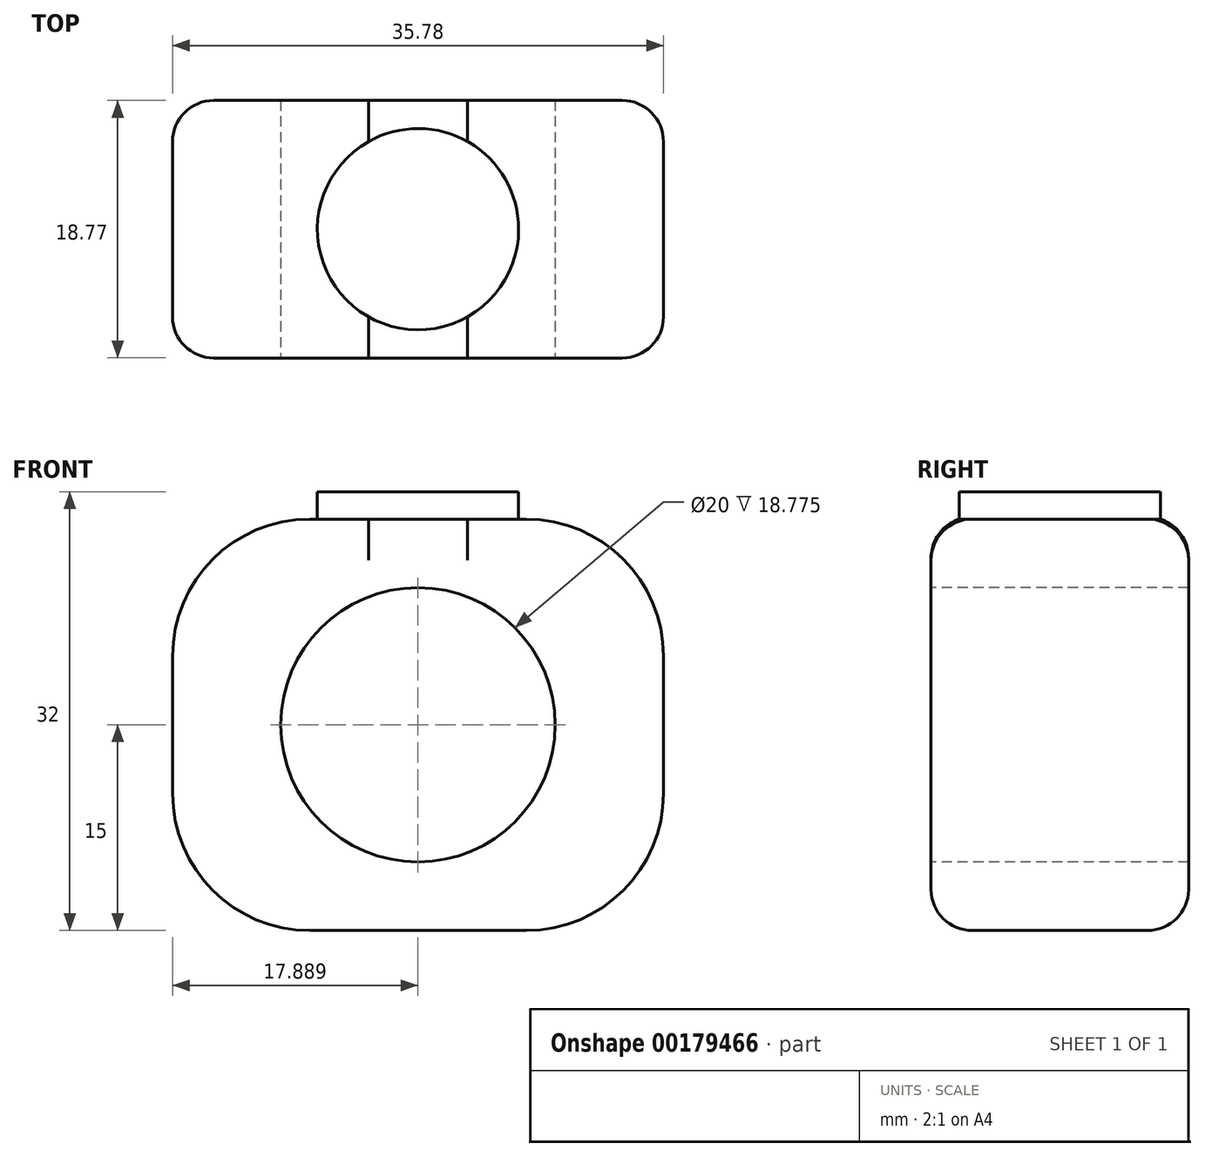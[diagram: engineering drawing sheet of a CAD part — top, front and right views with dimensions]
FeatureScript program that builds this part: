
annotation { "Feature Type Name" : "Feature", "Feature Type Description" : "" }
export const myFeature = defineFeature(function(context is Context, id is Id, definition is map)
    precondition{}
    {
        {
            var Q0;
            Q0=qCreatedBy(makeId("Top.planeOp"),FACE);
            var sketch = newSketch(context, id + "F0", { "sketchPlane" : qUnion([Q0])});
            skLineSegment(sketch, "E0.bottom", {"start": v(-30.93, 23.95) * mm, "end": v(4.85, 23.95) * mm});
            skLineSegment(sketch, "E0.top", {"start": v(-30.93, 5.18) * mm, "end": v(4.85, 5.18) * mm});
            skLineSegment(sketch, "E0.left", {"start": v(-30.93, 23.95) * mm, "end": v(-30.93, 5.18) * mm});
            skLineSegment(sketch, "E0.right", {"start": v(4.85, 23.95) * mm, "end": v(4.85, 5.18) * mm});
            skSolve(sketch);
        }
        {
            var Q0;
            Q0=makeQuery(id+"F0.imprint","IMPRINT",FACE,{"disambiguationData":[TD([[makeQuery(id+"F0.imprint","IMPRINT",EDGE,{"derivedFrom":sQuery(id+"F0.wireOp",EDGE,"E0.bottom")}),-1.0]])]});
            extrude(context, id + "F1", {"entities" : qUnion([Q0]), "depth" : 30 * mm});
        }
        {
            var Q0;
            Q0=makeQuery(id+"F1.opExtrude","SWEPT_FACE",FACE,{"disambiguationData":[OSD([sQuery(id+"F0.wireOp",EDGE,"E0.top")])]});
            var sketch = newSketch(context, id + "F2", { "sketchPlane" : qUnion([Q0])});
            skCircle(sketch, "E1", {"center": v(-13.04, 15) * mm, "radius": 10 * mm});
            skLineSegment(sketch, "E2", {"start": v(-30.93, 15) * mm, "end": v(4.85, 15) * mm});
            skLineSegment(sketch, "E3", {"start": v(-13.04, 15) * mm, "end": v(-13.04, -0.72) * mm});
            skSolve(sketch);
        }
        {
            var Q0;
            Q0=makeQuery(id+"F2.imprint","IMPRINT",FACE,{"disambiguationData":[TD([[makeQuery(id+"F2.imprint","IMPRINT",EDGE,{"derivedFrom":sQuery(id+"F2.wireOp",EDGE,"E1")}),1.0]])]});
            extrude(context, id + "F3", {"entities" : qUnion([Q0]), "operationType" : NewBodyOperationType.REMOVE, "oppositeDirection" : true, "depth" : 25 * mm});
        }
        {
            var Q0;
            Q0=makeQuery(id+"F1.opExtrude","CAP_FACE",FACE,{"disambiguationData":[OSD([sQuery(id+"F0.wireOp",EDGE,"E0.bottom"),sQuery(id+"F0.wireOp",EDGE,"E0.top"),sQuery(id+"F0.wireOp",EDGE,"E0.left"),sQuery(id+"F0.wireOp",EDGE,"E0.right")])],"isStart":false});
            var sketch = newSketch(context, id + "F4", { "sketchPlane" : qUnion([Q0])});
            skLineSegment(sketch, "E4", {"start": v(-30.93, 14.56) * mm, "end": v(4.85, 14.56) * mm});
            skCircle(sketch, "E5", {"center": v(-13.04, 14.56) * mm, "radius": 7.34 * mm});
            skSolve(sketch);
        }
        {
            var Q0;
            {var subQ0=sQuery(id+"F4.wireOp",EDGE,"E5");var subQ1=sQuery(id+"F4.wireOp",EDGE,"E4");var subQ2=makeQuery(id+"F4.imprint","INTERSECT",VERTEX,{"disambiguationData":[OD(0.0)],"derivedFrom":[subQ1,subQ0]});Q0=makeQuery(id+"F4.imprint","IMPRINT",FACE,{"disambiguationData":[TD([[makeQuery(id+"F4.imprint","IMPRINT",EDGE,{"disambiguationData":[TD([[subQ2,-1.0]])],"derivedFrom":subQ1}),1.0]])]});}
            var Q1;
            {var subQ0=sQuery(id+"F4.wireOp",EDGE,"E5");var subQ1=sQuery(id+"F4.wireOp",EDGE,"E4");var subQ2=makeQuery(id+"F4.imprint","INTERSECT",VERTEX,{"disambiguationData":[OD(0.0)],"derivedFrom":[subQ1,subQ0]});Q1=makeQuery(id+"F4.imprint","IMPRINT",FACE,{"disambiguationData":[TD([[makeQuery(id+"F4.imprint","IMPRINT",EDGE,{"disambiguationData":[TD([[subQ2,-1.0]])],"derivedFrom":subQ1}),-1.0]])]});}
            extrude(context, id + "F5", {"entities" : qUnion([Q0, Q1]), "operationType" : NewBodyOperationType.ADD, "depth" : 2 * mm});
        }
        {
            var Q0;
            Q0=makeQuery(id+"F1.opExtrude","CAP_EDGE",EDGE,{"disambiguationData":[OSD([sQuery(id+"F0.wireOp",EDGE,"E0.right")])],"isStart":false});
            var Q1;
            Q1=makeQuery(id+"F1.opExtrude","CAP_EDGE",EDGE,{"disambiguationData":[OSD([sQuery(id+"F0.wireOp",EDGE,"E0.left")])],"isStart":false});
            var Q2;
            Q2=makeQuery(id+"F1.opExtrude","CAP_EDGE",EDGE,{"disambiguationData":[OSD([sQuery(id+"F0.wireOp",EDGE,"E0.right")])],"isStart":true});
            var Q3;
            Q3=makeQuery(id+"F1.opExtrude","CAP_EDGE",EDGE,{"disambiguationData":[OSD([sQuery(id+"F0.wireOp",EDGE,"E0.left")])],"isStart":true});
            fillet(context, id + "F6", {"entities" : qUnion([Q0, Q1, Q2, Q3]), "radius" : 10 * mm, "tangentPropagation" : true, "allowEdgeOverflow" : false});
        }
        {
            var Q0;
            Q0=makeQuery(id+"F6.opFillet","BLEND_EDGE",EDGE,{"blendedFrom":[makeQuery(id+"F1.opExtrude","CAP_EDGE",EDGE,{"disambiguationData":[OSD([sQuery(id+"F0.wireOp",EDGE,"E0.right")])],"isStart":false}),makeQuery(id+"F1.opExtrude","SWEPT_FACE",FACE,{"disambiguationData":[OSD([sQuery(id+"F0.wireOp",EDGE,"E0.top")])]})],"blendedInto":[makeQuery(id+"F1.opExtrude","SWEPT_FACE",FACE,{"disambiguationData":[OSD([sQuery(id+"F0.wireOp",EDGE,"E0.top")])]})]});
            var Q1;
            Q1=makeQuery(id+"F6.opFillet","BLEND_EDGE",EDGE,{"blendedFrom":[makeQuery(id+"F1.opExtrude","CAP_EDGE",EDGE,{"disambiguationData":[OSD([sQuery(id+"F0.wireOp",EDGE,"E0.right")])],"isStart":false}),makeQuery(id+"F1.opExtrude","SWEPT_FACE",FACE,{"disambiguationData":[OSD([sQuery(id+"F0.wireOp",EDGE,"E0.bottom")])]})],"blendedInto":[makeQuery(id+"F1.opExtrude","SWEPT_FACE",FACE,{"disambiguationData":[OSD([sQuery(id+"F0.wireOp",EDGE,"E0.bottom")])]})]});
            fillet(context, id + "F7", {"entities" : qUnion([Q0, Q1]), "radius" : 3 * mm, "tangentPropagation" : true, "allowEdgeOverflow" : false});
        }
    });
